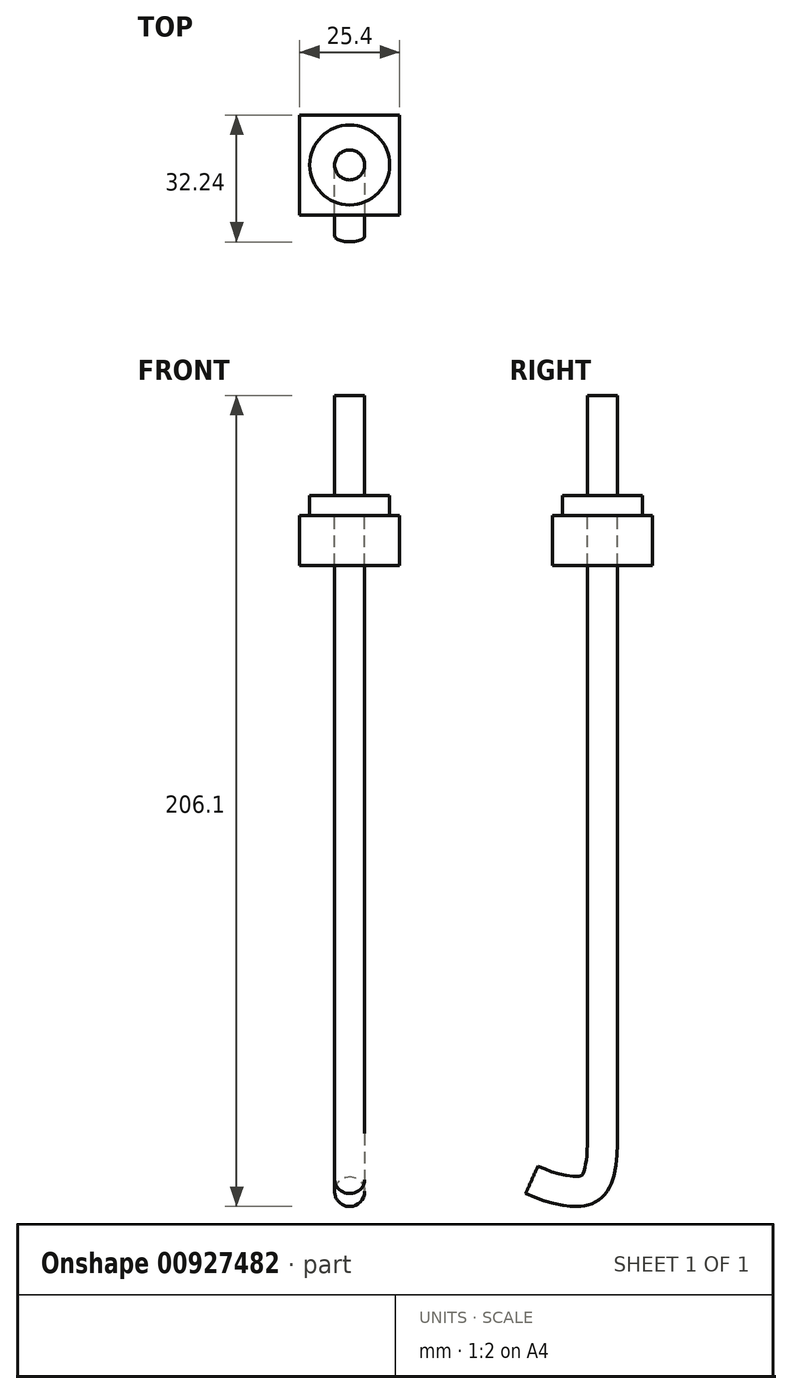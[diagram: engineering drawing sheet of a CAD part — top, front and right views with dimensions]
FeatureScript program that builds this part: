
annotation { "Feature Type Name" : "Feature", "Feature Type Description" : "" }
export const myFeature = defineFeature(function(context is Context, id is Id, definition is map)
    precondition{}
    {
        {
            var Q0;
            Q0=qCreatedBy(makeId("Top.planeOp"),FACE);
            var sketch = newSketch(context, id + "F0", { "sketchPlane" : qUnion([Q0])});
            skLineSegment(sketch, "E0.bottom", {"start": v(12.7, 12.7) * mm, "end": v(-12.7, 12.7) * mm});
            skLineSegment(sketch, "E0.top", {"start": v(12.7, -12.7) * mm, "end": v(-12.7, -12.7) * mm});
            skLineSegment(sketch, "E0.left", {"start": v(12.7, 12.7) * mm, "end": v(12.7, -12.7) * mm});
            skLineSegment(sketch, "E0.right", {"start": v(-12.7, 12.7) * mm, "end": v(-12.7, -12.7) * mm});
            skPoint(sketch, "E0.middle", {"position": v(0, 0) * mm});
            skSolve(sketch);
        }
        {
            var Q0;
            Q0 = qSketchRegion(id + "F0", true);
            extrude(context, id + "F1", {"entities" : qUnion([Q0]), "depth" : 12.7 * mm, "offsetDistance" : 25.4 * mm});
        }
        {
            var Q0;
            Q0=makeQuery(id+"F1.opExtrude","CAP_FACE",FACE,{"disambiguationData":[OSD([sQuery(id+"F0.wireOp",EDGE,"E0.bottom"),sQuery(id+"F0.wireOp",EDGE,"E0.top"),sQuery(id+"F0.wireOp",EDGE,"E0.left"),sQuery(id+"F0.wireOp",EDGE,"E0.right")])],"isStart":false});
            var sketch = newSketch(context, id + "F2", { "sketchPlane" : qUnion([Q0])});
            skSolve(sketch);
        }
        {
            var Q0;
            Q0=makeQuery(id+"F2.imprint","IMPRINT",FACE,{"disambiguationData":[TD([[makeQuery(id+"F2.imprint","IMPRINT",EDGE,{"derivedFrom":makeQuery(id+"F1.opExtrude","CAP_EDGE",EDGE,{"disambiguationData":[OSD([sQuery(id+"F0.wireOp",EDGE,"E0.bottom")])],"isStart":false})}),1.0]])]});
            var sketch = newSketch(context, id + "F3", { "sketchPlane" : qUnion([Q0])});
            skCircle(sketch, "E1", {"center": v(0, 0) * mm, "radius": 10.16 * mm});
            skCircle(sketch, "E2", {"center": v(0, 0) * mm, "radius": 3.81 * mm});
            skSolve(sketch);
        }
        {
            var Q0;
            Q0 = qSketchRegion(id + "F3", true);
            extrude(context, id + "F4", {"entities" : qUnion([Q0]), "depth" : 5.08 * mm, "offsetDistance" : 25.4 * mm});
        }
        {
            var Q0;
            Q0=makeQuery(id+"F4.opExtrude","CAP_FACE",FACE,{"disambiguationData":[OSD([sQuery(id+"F3.wireOp",EDGE,"E1"),sQuery(id+"F3.wireOp",EDGE,"E2")])],"isStart":false});
            var sketch = newSketch(context, id + "F5", { "sketchPlane" : qUnion([Q0])});
            skCircle(sketch, "E3.0", {"center": v(0, 0) * mm, "radius": 3.81 * mm});
            skSolve(sketch);
        }
        {
            var Q0;
            Q0 = qSketchRegion(id + "F5", true);
            extrude(context, id + "F6", {"entities" : qUnion([Q0]), "oppositeDirection" : true, "depth" : 152.4 * mm, "offsetDistance" : 25.4 * mm});
        }
        {
            var Q0;
            Q0 = qSketchRegion(id + "F5", true);
            extrude(context, id + "F7", {"entities" : qUnion([Q0]), "operationType" : NewBodyOperationType.ADD, "depth" : 25.4 * mm, "offsetDistance" : 25.4 * mm});
        }
        {
            var Q0;
            Q0=qCreatedBy(makeId("Right.planeOp"),FACE);
            var sketch = newSketch(context, id + "F8", { "sketchPlane" : qUnion([Q0])});
            skLineSegment(sketch, "E4", {"start": v(0, -132.84) * mm, "end": v(0, -144.39) * mm});
            skFitSpline(sketch, "E5", {"points": [v(0, -144.39) * mm, v(-5, -158.92) * mm, v(-17.98, -156.14) * mm], "startDerivative": vector(0, -62.67) * mm, "endDerivative": vector(-31.14, 13.93) * mm});
            skSolve(sketch);
        }
        {
            var Q0;
            Q0=makeQuery(id+"F6.opExtrude","CAP_FACE",FACE,{"disambiguationData":[OSD([sQuery(id+"F5.wireOp",EDGE,"E3.0")])],"isStart":false});
            var Q1;
            Q1=sQuery(id+"F8.wireOp",EDGE,"E4");
            var Q2;
            Q2=sQuery(id+"F8.wireOp",EDGE,"E5");
            sweep(context, id + "F9", {"operationType" : NewBodyOperationType.ADD, "profiles" : qUnion([Q0]), "path" : qUnion([Q1, Q2])});
        }
    });
